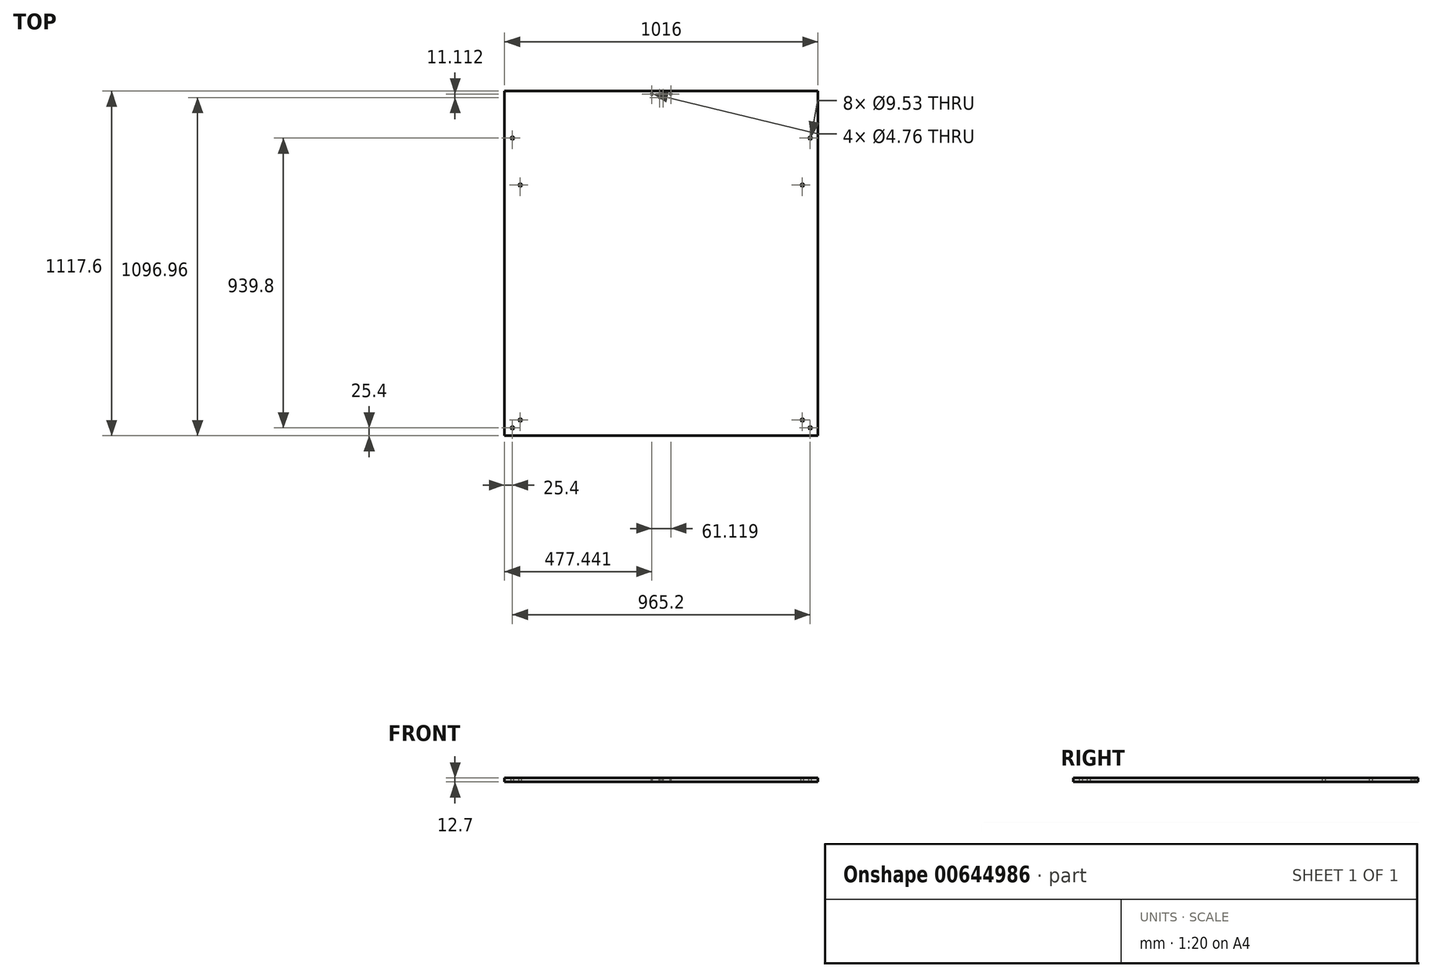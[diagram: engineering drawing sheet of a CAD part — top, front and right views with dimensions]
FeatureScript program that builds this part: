
annotation { "Feature Type Name" : "Feature", "Feature Type Description" : "" }
export const myFeature = defineFeature(function(context is Context, id is Id, definition is map)
    precondition{}
    {
        {
            var Q0;
            Q0=qCreatedBy(makeId("Top.planeOp"),FACE);
            var sketch = newSketch(context, id + "F0", { "sketchPlane" : qUnion([Q0])});
            skLineSegment(sketch, "E0.bottom", {"start": v(508, -558.8) * mm, "end": v(-508, -558.8) * mm});
            skLineSegment(sketch, "E0.top", {"start": v(508, 558.8) * mm, "end": v(-508, 558.8) * mm});
            skLineSegment(sketch, "E0.left", {"start": v(508, -558.8) * mm, "end": v(508, 558.8) * mm});
            skLineSegment(sketch, "E0.right", {"start": v(-508, -558.8) * mm, "end": v(-508, 558.8) * mm});
            skPoint(sketch, "E0.middle", {"position": v(0, 0) * mm});
            skSolve(sketch);
        }
        {
            var Q0;
            Q0=makeQuery(id+"F0.imprint","IMPRINT",FACE,{"disambiguationData":[TD([[makeQuery(id+"F0.imprint","IMPRINT",EDGE,{"derivedFrom":sQuery(id+"F0.wireOp",EDGE,"E0.bottom")}),-1.0]])]});
            extrude(context, id + "F1", {"entities" : qUnion([Q0]), "depth" : 12.7 * mm, "offsetDistance" : 25.4 * mm});
        }
        {
            var Q0;
            Q0=makeQuery(id+"F1.opExtrude","CAP_FACE",FACE,{"disambiguationData":[OSD([sQuery(id+"F0.wireOp",EDGE,"E0.bottom"),sQuery(id+"F0.wireOp",EDGE,"E0.top"),sQuery(id+"F0.wireOp",EDGE,"E0.left"),sQuery(id+"F0.wireOp",EDGE,"E0.right")])],"isStart":false});
            var sketch = newSketch(context, id + "F2", { "sketchPlane" : qUnion([Q0])});
            skLineSegment(sketch, "E1.bottom", {"start": v(-508, 558.8) * mm, "end": v(0, 558.8) * mm});
            skLineSegment(sketch, "E1.top", {"start": v(-508, 552.45) * mm, "end": v(0, 552.45) * mm});
            skLineSegment(sketch, "E1.left", {"start": v(-508, 558.8) * mm, "end": v(-508, 552.45) * mm});
            skLineSegment(sketch, "E1.right", {"start": v(0, 558.8) * mm, "end": v(0, 552.45) * mm});
            skLineSegment(sketch, "E2.bottom", {"start": v(30.56, 568.33) * mm, "end": v(-30.56, 568.33) * mm});
            skLineSegment(sketch, "E2.top", {"start": v(30.56, 549.28) * mm, "end": v(-30.56, 549.28) * mm});
            skLineSegment(sketch, "E2.left", {"start": v(30.56, 568.33) * mm, "end": v(30.56, 549.28) * mm});
            skLineSegment(sketch, "E2.right", {"start": v(-30.56, 568.33) * mm, "end": v(-30.56, 549.28) * mm});
            skPoint(sketch, "E2.middle", {"position": v(0, 558.8) * mm});
            skCircle(sketch, "E3", {"center": v(-30.56, 549.28) * mm, "radius": 2.38 * mm});
            skCircle(sketch, "E4", {"center": v(30.56, 549.28) * mm, "radius": 2.38 * mm});
            skLineSegment(sketch, "E5.bottom", {"start": v(12.7, 555.62) * mm, "end": v(-12.7, 555.62) * mm});
            skLineSegment(sketch, "E5.top", {"start": v(12.7, 549.28) * mm, "end": v(-12.7, 549.28) * mm});
            skLineSegment(sketch, "E5.left", {"start": v(12.7, 555.62) * mm, "end": v(12.7, 549.28) * mm});
            skLineSegment(sketch, "E5.right", {"start": v(-12.7, 555.62) * mm, "end": v(-12.7, 549.28) * mm});
            skPoint(sketch, "E5.middle", {"position": v(0, 552.45) * mm});
            skLineSegment(sketch, "E6", {"start": v(-30.56, 549.28) * mm, "end": v(-30.56, 538.16) * mm});
            skLineSegment(sketch, "E7", {"start": v(-30.56, 538.16) * mm, "end": v(-5.16, 538.16) * mm});
            skLineSegment(sketch, "E8", {"start": v(30.56, 549.28) * mm, "end": v(30.56, 538.16) * mm});
            skLineSegment(sketch, "E9", {"start": v(30.56, 538.16) * mm, "end": v(5.16, 538.16) * mm});
            skLineSegment(sketch, "E10", {"start": v(5.16, 538.16) * mm, "end": v(-5.16, 538.16) * mm});
            skCircle(sketch, "E11", {"center": v(-5.16, 538.16) * mm, "radius": 2.38 * mm});
            skCircle(sketch, "E12", {"center": v(5.16, 538.16) * mm, "radius": 2.38 * mm});
            skSolve(sketch);
        }
        {
            var Q0;
            {var subQ1=sQuery(id+"F2.wireOp",EDGE,"E2.right");var subQ3=sQuery(id+"F2.wireOp",EDGE,"E3");var subQ4=makeQuery(id+"F2.imprint","INTERSECT",VERTEX,{"derivedFrom":[subQ1,subQ3]});Q0=makeQuery(id+"F2.imprint","IMPRINT",FACE,{"disambiguationData":[TD([[makeQuery(id+"F2.imprint","IMPRINT",EDGE,{"disambiguationData":[TD([[subQ4,-1.0]])],"derivedFrom":subQ3}),1.0]])]});}
            var Q1;
            {var subQ1=sQuery(id+"F2.wireOp",EDGE,"E2.top");var subQ3=sQuery(id+"F2.wireOp",EDGE,"E3");var subQ4=makeQuery(id+"F2.imprint","INTERSECT",VERTEX,{"derivedFrom":[subQ1,subQ3]});Q1=makeQuery(id+"F2.imprint","IMPRINT",FACE,{"disambiguationData":[TD([[makeQuery(id+"F2.imprint","IMPRINT",EDGE,{"disambiguationData":[TD([[subQ4,-1.0]])],"derivedFrom":subQ3}),1.0]])]});}
            var Q2;
            {var subQ1=sQuery(id+"F2.wireOp",EDGE,"E2.top");var subQ3=sQuery(id+"F2.wireOp",EDGE,"E3");var subQ4=makeQuery(id+"F2.imprint","INTERSECT",VERTEX,{"derivedFrom":[subQ1,subQ3]});Q2=makeQuery(id+"F2.imprint","IMPRINT",FACE,{"disambiguationData":[TD([[makeQuery(id+"F2.imprint","IMPRINT",EDGE,{"disambiguationData":[TD([[subQ4,1.0]])],"derivedFrom":subQ3}),1.0]])]});}
            var Q3;
            {var subQ0=sQuery(id+"F2.wireOp",EDGE,"E10");var subQ1=sQuery(id+"F2.wireOp",EDGE,"E7");var subQ2=makeQuery(id+"F2.imprint","INTERSECT",VERTEX,{"derivedFrom":[subQ1,subQ0]});Q3=makeQuery(id+"F2.imprint","IMPRINT",FACE,{"disambiguationData":[TD([[makeQuery(id+"F2.imprint","IMPRINT",EDGE,{"disambiguationData":[TD([[subQ2,1.0]])],"derivedFrom":subQ1}),-1.0]])]});}
            var Q4;
            {var subQ0=sQuery(id+"F2.wireOp",EDGE,"E10");var subQ1=sQuery(id+"F2.wireOp",EDGE,"E7");var subQ2=makeQuery(id+"F2.imprint","INTERSECT",VERTEX,{"derivedFrom":[subQ1,subQ0]});Q4=makeQuery(id+"F2.imprint","IMPRINT",FACE,{"disambiguationData":[TD([[makeQuery(id+"F2.imprint","IMPRINT",EDGE,{"disambiguationData":[TD([[subQ2,1.0]])],"derivedFrom":subQ1}),1.0]])]});}
            var Q5;
            {var subQ0=sQuery(id+"F2.wireOp",EDGE,"E10");var subQ1=sQuery(id+"F2.wireOp",EDGE,"E9");var subQ2=makeQuery(id+"F2.imprint","INTERSECT",VERTEX,{"derivedFrom":[subQ1,subQ0]});Q5=makeQuery(id+"F2.imprint","IMPRINT",FACE,{"disambiguationData":[TD([[makeQuery(id+"F2.imprint","IMPRINT",EDGE,{"disambiguationData":[TD([[subQ2,1.0]])],"derivedFrom":subQ1}),-1.0]])]});}
            var Q6;
            {var subQ0=sQuery(id+"F2.wireOp",EDGE,"E10");var subQ1=sQuery(id+"F2.wireOp",EDGE,"E9");var subQ2=makeQuery(id+"F2.imprint","INTERSECT",VERTEX,{"derivedFrom":[subQ1,subQ0]});Q6=makeQuery(id+"F2.imprint","IMPRINT",FACE,{"disambiguationData":[TD([[makeQuery(id+"F2.imprint","IMPRINT",EDGE,{"disambiguationData":[TD([[subQ2,1.0]])],"derivedFrom":subQ1}),1.0]])]});}
            var Q7;
            {var subQ1=sQuery(id+"F2.wireOp",EDGE,"E2.top");var subQ3=sQuery(id+"F2.wireOp",EDGE,"E4");var subQ4=makeQuery(id+"F2.imprint","INTERSECT",VERTEX,{"derivedFrom":[subQ1,subQ3]});Q7=makeQuery(id+"F2.imprint","IMPRINT",FACE,{"disambiguationData":[TD([[makeQuery(id+"F2.imprint","IMPRINT",EDGE,{"disambiguationData":[TD([[subQ4,1.0]])],"derivedFrom":subQ3}),1.0]])]});}
            var Q8;
            {var subQ1=sQuery(id+"F2.wireOp",EDGE,"E2.top");var subQ3=sQuery(id+"F2.wireOp",EDGE,"E4");var subQ4=makeQuery(id+"F2.imprint","INTERSECT",VERTEX,{"derivedFrom":[subQ1,subQ3]});Q8=makeQuery(id+"F2.imprint","IMPRINT",FACE,{"disambiguationData":[TD([[makeQuery(id+"F2.imprint","IMPRINT",EDGE,{"disambiguationData":[TD([[subQ4,-1.0]])],"derivedFrom":subQ3}),1.0]])]});}
            var Q9;
            {var subQ1=sQuery(id+"F2.wireOp",EDGE,"E2.left");var subQ3=sQuery(id+"F2.wireOp",EDGE,"E4");var subQ4=makeQuery(id+"F2.imprint","INTERSECT",VERTEX,{"derivedFrom":[subQ1,subQ3]});Q9=makeQuery(id+"F2.imprint","IMPRINT",FACE,{"disambiguationData":[TD([[makeQuery(id+"F2.imprint","IMPRINT",EDGE,{"disambiguationData":[TD([[subQ4,1.0]])],"derivedFrom":subQ3}),1.0]])]});}
            var Q10;
            {var subQ1=sQuery(id+"F2.wireOp",EDGE,"E1.top");var subQ3=sQuery(id+"F2.wireOp",EDGE,"E3");var subQ4=makeQuery(id+"F2.imprint","INTERSECT",VERTEX,{"derivedFrom":[subQ1,subQ3]});Q10=makeQuery(id+"F2.imprint","IMPRINT",FACE,{"disambiguationData":[TD([[makeQuery(id+"F2.imprint","IMPRINT",EDGE,{"disambiguationData":[TD([[subQ4,-1.0]])],"derivedFrom":subQ3}),1.0]])]});}
            extrude(context, id + "F3", {"entities" : qUnion([Q0, Q1, Q2, Q3, Q4, Q5, Q6, Q7, Q8, Q9, Q10]), "operationType" : NewBodyOperationType.REMOVE, "oppositeDirection" : true, "depth" : 25.4 * mm, "offsetDistance" : 25.4 * mm});
        }
        {
            var Q0;
            Q0=makeQuery(id+"F1.opExtrude","CAP_FACE",FACE,{"disambiguationData":[OSD([sQuery(id+"F0.wireOp",EDGE,"E0.bottom"),sQuery(id+"F0.wireOp",EDGE,"E0.top"),sQuery(id+"F0.wireOp",EDGE,"E0.left"),sQuery(id+"F0.wireOp",EDGE,"E0.right")])],"isStart":false});
            var sketch = newSketch(context, id + "F4", { "sketchPlane" : qUnion([Q0])});
            skLineSegment(sketch, "E13.bottom", {"start": v(-508, -558.8) * mm, "end": v(-457.2, -558.8) * mm});
            skLineSegment(sketch, "E13.top", {"start": v(-508, -508) * mm, "end": v(-457.2, -508) * mm});
            skLineSegment(sketch, "E13.left", {"start": v(-508, -558.8) * mm, "end": v(-508, -508) * mm});
            skLineSegment(sketch, "E13.right", {"start": v(-457.2, -558.8) * mm, "end": v(-457.2, -508) * mm});
            skCircle(sketch, "E14", {"center": v(-457.2, -508) * mm, "radius": 4.76 * mm});
            skCircle(sketch, "E15", {"center": v(-482.6, -533.4) * mm, "radius": 4.76 * mm});
            skPoint(sketch, "E15.centerSnap0", {"position": v(-482.6, -508) * mm});
            skPoint(sketch, "E15.centerSnap1", {"position": v(-508, -533.4) * mm});
            skLineSegment(sketch, "E16.bottom", {"start": v(508, -558.8) * mm, "end": v(457.2, -558.8) * mm});
            skLineSegment(sketch, "E16.top", {"start": v(508, -508) * mm, "end": v(457.2, -508) * mm});
            skLineSegment(sketch, "E16.left", {"start": v(508, -558.8) * mm, "end": v(508, -508) * mm});
            skLineSegment(sketch, "E16.right", {"start": v(457.2, -558.8) * mm, "end": v(457.2, -508) * mm});
            skCircle(sketch, "E17", {"center": v(457.2, -508) * mm, "radius": 4.76 * mm});
            skCircle(sketch, "E18", {"center": v(482.6, -533.4) * mm, "radius": 4.76 * mm});
            skPoint(sketch, "E18.centerSnap0", {"position": v(457.2, -533.4) * mm});
            skPoint(sketch, "E18.centerSnap1", {"position": v(482.6, -508) * mm});
            skLineSegment(sketch, "E19.bottom", {"start": v(508, 558.8) * mm, "end": v(457.2, 558.8) * mm});
            skLineSegment(sketch, "E19.top", {"start": v(508, 254) * mm, "end": v(457.2, 254) * mm});
            skLineSegment(sketch, "E19.left", {"start": v(508, 558.8) * mm, "end": v(508, 254) * mm});
            skLineSegment(sketch, "E19.right", {"start": v(457.2, 558.8) * mm, "end": v(457.2, 254) * mm});
            skCircle(sketch, "E20", {"center": v(457.2, 254) * mm, "radius": 4.76 * mm});
            skCircle(sketch, "E21", {"center": v(482.6, 406.4) * mm, "radius": 4.76 * mm});
            skPoint(sketch, "E21.centerSnap0", {"position": v(482.6, 254) * mm});
            skPoint(sketch, "E21.centerSnap1", {"position": v(457.2, 406.4) * mm});
            skLineSegment(sketch, "E22.bottom", {"start": v(-508, 558.8) * mm, "end": v(-457.2, 558.8) * mm});
            skLineSegment(sketch, "E22.top", {"start": v(-508, 254) * mm, "end": v(-457.2, 254) * mm});
            skLineSegment(sketch, "E22.left", {"start": v(-508, 558.8) * mm, "end": v(-508, 254) * mm});
            skLineSegment(sketch, "E22.right", {"start": v(-457.2, 558.8) * mm, "end": v(-457.2, 254) * mm});
            skCircle(sketch, "E23", {"center": v(-457.2, 254) * mm, "radius": 4.76 * mm});
            skCircle(sketch, "E24", {"center": v(-482.6, 406.4) * mm, "radius": 4.76 * mm});
            skPoint(sketch, "E24.centerSnap0", {"position": v(-482.6, 254) * mm});
            skPoint(sketch, "E24.centerSnap1", {"position": v(-457.2, 406.4) * mm});
            skSolve(sketch);
        }
        {
            var Q0;
            Q0=makeQuery(id+"F4.imprint","IMPRINT",FACE,{"disambiguationData":[TD([[makeQuery(id+"F4.imprint","IMPRINT",EDGE,{"derivedFrom":sQuery(id+"F4.wireOp",EDGE,"E24")}),1.0]])]});
            var Q1;
            {var subQ0=sQuery(id+"F4.wireOp",EDGE,"E22.right");var subQ1=sQuery(id+"F4.wireOp",EDGE,"E22.top");var subQ2=makeQuery(id+"F4.imprint","INTERSECT",VERTEX,{"derivedFrom":[subQ1,subQ0]});Q1=makeQuery(id+"F4.imprint","IMPRINT",FACE,{"disambiguationData":[TD([[makeQuery(id+"F4.imprint","IMPRINT",EDGE,{"disambiguationData":[TD([[subQ2,1.0]])],"derivedFrom":subQ1}),-1.0]])]});}
            var Q2;
            {var subQ0=sQuery(id+"F4.wireOp",EDGE,"E22.right");var subQ1=sQuery(id+"F4.wireOp",EDGE,"E22.top");var subQ2=makeQuery(id+"F4.imprint","INTERSECT",VERTEX,{"derivedFrom":[subQ1,subQ0]});Q2=makeQuery(id+"F4.imprint","IMPRINT",FACE,{"disambiguationData":[TD([[makeQuery(id+"F4.imprint","IMPRINT",EDGE,{"disambiguationData":[TD([[subQ2,1.0]])],"derivedFrom":subQ1}),1.0]])]});}
            var Q3;
            Q3=makeQuery(id+"F4.imprint","IMPRINT",FACE,{"disambiguationData":[TD([[makeQuery(id+"F4.imprint","IMPRINT",EDGE,{"derivedFrom":sQuery(id+"F4.wireOp",EDGE,"E15")}),1.0]])]});
            var Q4;
            {var subQ0=sQuery(id+"F4.wireOp",EDGE,"E13.right");var subQ1=sQuery(id+"F4.wireOp",EDGE,"E13.top");var subQ2=makeQuery(id+"F4.imprint","INTERSECT",VERTEX,{"derivedFrom":[subQ1,subQ0]});Q4=makeQuery(id+"F4.imprint","IMPRINT",FACE,{"disambiguationData":[TD([[makeQuery(id+"F4.imprint","IMPRINT",EDGE,{"disambiguationData":[TD([[subQ2,1.0]])],"derivedFrom":subQ1}),1.0]])]});}
            var Q5;
            {var subQ0=sQuery(id+"F4.wireOp",EDGE,"E13.right");var subQ1=sQuery(id+"F4.wireOp",EDGE,"E13.top");var subQ2=makeQuery(id+"F4.imprint","INTERSECT",VERTEX,{"derivedFrom":[subQ1,subQ0]});Q5=makeQuery(id+"F4.imprint","IMPRINT",FACE,{"disambiguationData":[TD([[makeQuery(id+"F4.imprint","IMPRINT",EDGE,{"disambiguationData":[TD([[subQ2,1.0]])],"derivedFrom":subQ1}),-1.0]])]});}
            var Q6;
            Q6=makeQuery(id+"F4.imprint","IMPRINT",FACE,{"disambiguationData":[TD([[makeQuery(id+"F4.imprint","IMPRINT",EDGE,{"derivedFrom":sQuery(id+"F4.wireOp",EDGE,"E18")}),1.0]])]});
            var Q7;
            {var subQ0=sQuery(id+"F4.wireOp",EDGE,"E16.right");var subQ1=sQuery(id+"F4.wireOp",EDGE,"E16.top");var subQ2=makeQuery(id+"F4.imprint","INTERSECT",VERTEX,{"derivedFrom":[subQ1,subQ0]});Q7=makeQuery(id+"F4.imprint","IMPRINT",FACE,{"disambiguationData":[TD([[makeQuery(id+"F4.imprint","IMPRINT",EDGE,{"disambiguationData":[TD([[subQ2,1.0]])],"derivedFrom":subQ1}),1.0]])]});}
            var Q8;
            {var subQ0=sQuery(id+"F4.wireOp",EDGE,"E16.right");var subQ1=sQuery(id+"F4.wireOp",EDGE,"E16.top");var subQ2=makeQuery(id+"F4.imprint","INTERSECT",VERTEX,{"derivedFrom":[subQ1,subQ0]});Q8=makeQuery(id+"F4.imprint","IMPRINT",FACE,{"disambiguationData":[TD([[makeQuery(id+"F4.imprint","IMPRINT",EDGE,{"disambiguationData":[TD([[subQ2,1.0]])],"derivedFrom":subQ1}),-1.0]])]});}
            var Q9;
            {var subQ0=sQuery(id+"F4.wireOp",EDGE,"E19.right");var subQ1=sQuery(id+"F4.wireOp",EDGE,"E19.top");var subQ2=makeQuery(id+"F4.imprint","INTERSECT",VERTEX,{"derivedFrom":[subQ1,subQ0]});Q9=makeQuery(id+"F4.imprint","IMPRINT",FACE,{"disambiguationData":[TD([[makeQuery(id+"F4.imprint","IMPRINT",EDGE,{"disambiguationData":[TD([[subQ2,1.0]])],"derivedFrom":subQ1}),1.0]])]});}
            var Q10;
            {var subQ0=sQuery(id+"F4.wireOp",EDGE,"E19.right");var subQ1=sQuery(id+"F4.wireOp",EDGE,"E19.top");var subQ2=makeQuery(id+"F4.imprint","INTERSECT",VERTEX,{"derivedFrom":[subQ1,subQ0]});Q10=makeQuery(id+"F4.imprint","IMPRINT",FACE,{"disambiguationData":[TD([[makeQuery(id+"F4.imprint","IMPRINT",EDGE,{"disambiguationData":[TD([[subQ2,1.0]])],"derivedFrom":subQ1}),-1.0]])]});}
            var Q11;
            Q11=makeQuery(id+"F4.imprint","IMPRINT",FACE,{"disambiguationData":[TD([[makeQuery(id+"F4.imprint","IMPRINT",EDGE,{"derivedFrom":sQuery(id+"F4.wireOp",EDGE,"E21")}),1.0]])]});
            extrude(context, id + "F5", {"entities" : qUnion([Q0, Q1, Q2, Q3, Q4, Q5, Q6, Q7, Q8, Q9, Q10, Q11]), "operationType" : NewBodyOperationType.REMOVE, "oppositeDirection" : true, "depth" : 25.4 * mm, "offsetDistance" : 25.4 * mm});
        }
    });
